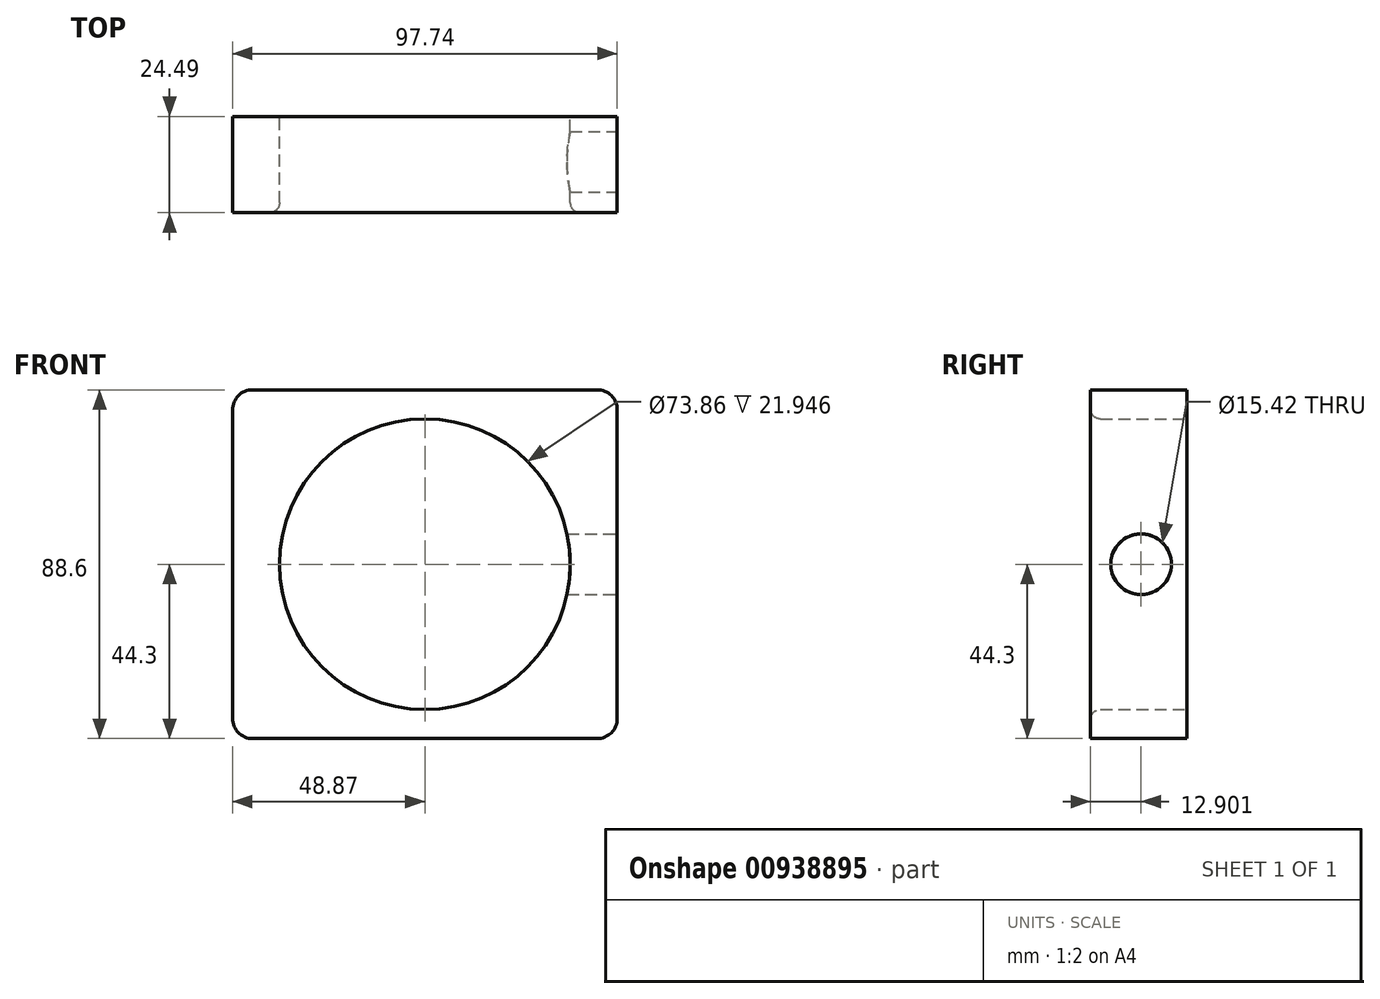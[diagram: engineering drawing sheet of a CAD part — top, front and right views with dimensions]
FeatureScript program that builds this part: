
annotation { "Feature Type Name" : "Feature", "Feature Type Description" : "" }
export const myFeature = defineFeature(function(context is Context, id is Id, definition is map)
    precondition{}
    {
        {
            var Q0;
            Q0=qCreatedBy(makeId("Front.planeOp"),FACE);
            var sketch = newSketch(context, id + "F0", { "sketchPlane" : qUnion([Q0])});
            skLineSegment(sketch, "E0.bottom", {"start": v(48.87, 44.3) * mm, "end": v(-48.87, 44.3) * mm});
            skLineSegment(sketch, "E0.top", {"start": v(48.87, -44.3) * mm, "end": v(-48.87, -44.3) * mm});
            skLineSegment(sketch, "E0.left", {"start": v(48.87, 44.3) * mm, "end": v(48.87, -44.3) * mm});
            skLineSegment(sketch, "E0.right", {"start": v(-48.87, 44.3) * mm, "end": v(-48.87, -44.3) * mm});
            skPoint(sketch, "E0.middle", {"position": v(0, 0) * mm});
            skCircle(sketch, "E1", {"center": v(0, 0) * mm, "radius": 36.93 * mm});
            skSolve(sketch);
        }
        {
            var Q0;
            Q0 = qSketchRegion(id + "F0", true);
            extrude(context, id + "F1", {"entities" : qUnion([Q0]), "depth" : 24.49 * mm, "offsetDistance" : 25.4 * mm});
        }
        {
            var Q0;
            Q0=makeQuery(id+"F1.opExtrude","SWEPT_EDGE",EDGE,{"disambiguationData":[OSD([sQuery(id+"F0.wireOp",EDGE,"E0.bottom"),sQuery(id+"F0.wireOp",EDGE,"E0.left")])]});
            var Q1;
            Q1=makeQuery(id+"F1.opExtrude","SWEPT_EDGE",EDGE,{"disambiguationData":[OSD([sQuery(id+"F0.wireOp",EDGE,"E0.top"),sQuery(id+"F0.wireOp",EDGE,"E0.left")])]});
            var Q2;
            Q2=makeQuery(id+"F1.opExtrude","SWEPT_EDGE",EDGE,{"disambiguationData":[OSD([sQuery(id+"F0.wireOp",EDGE,"E0.bottom"),sQuery(id+"F0.wireOp",EDGE,"E0.right")])]});
            var Q3;
            Q3=makeQuery(id+"F1.opExtrude","SWEPT_EDGE",EDGE,{"disambiguationData":[OSD([sQuery(id+"F0.wireOp",EDGE,"E0.top"),sQuery(id+"F0.wireOp",EDGE,"E0.right")])]});
            fillet(context, id + "F2", {"entities" : qUnion([Q0, Q1, Q2, Q3]), "radius" : 5.08 * mm, "tangentPropagation" : true, "allowEdgeOverflow" : false});
        }
        {
            var Q0;
            Q0=makeQuery(id+"F1.opExtrude","SWEPT_FACE",FACE,{"disambiguationData":[OSD([sQuery(id+"F0.wireOp",EDGE,"E0.left")])]});
            var sketch = newSketch(context, id + "F3", { "sketchPlane" : qUnion([Q0])});
            skPoint(sketch, "E2", {"position": v(-11.59, 0) * mm});
            skCircle(sketch, "E3", {"center": v(-11.59, 0) * mm, "radius": 7.7 * mm});
            skSolve(sketch);
        }
        {
            var Q0;
            Q0=makeQuery(id+"F3.imprint","IMPRINT",FACE,{"disambiguationData":[TD([[makeQuery(id+"F3.imprint","IMPRINT",EDGE,{"derivedFrom":sQuery(id+"F3.wireOp",EDGE,"E3")}),1.0]])]});
            extrude(context, id + "F4", {"entities" : qUnion([Q0]), "operationType" : NewBodyOperationType.REMOVE, "oppositeDirection" : true, "depth" : 25.4 * mm, "offsetDistance" : 25.4 * mm});
        }
        {
            var Q0;
            Q0=makeQuery(id+"F1.opExtrude","CAP_EDGE",EDGE,{"disambiguationData":[OSD([sQuery(id+"F0.wireOp",EDGE,"E1")])],"isStart":false});
            fillet(context, id + "F5", {"entities" : qUnion([Q0]), "radius" : 2.54 * mm, "tangentPropagation" : true, "allowEdgeOverflow" : false});
        }
    });
